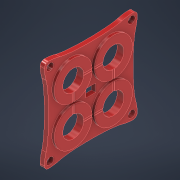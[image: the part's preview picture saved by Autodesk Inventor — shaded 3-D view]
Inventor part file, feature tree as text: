
AUTODESK INVENTOR PART (.ipt)
format: ipt  version: 2022 (Build 260153000, 153)  size: 302,080 bytes
history: native  units: mm
features: extrude x5, projected_geometry x5, sketch x4, fillet x2
ambient origin geometry x8: Origin, YZ Plane, XZ Plane, XY Plane, X Axis, Y Axis, Z Axis, Center Point
bodies: Solid1 (feature_tree)
feature tree (16):
  extrude  "Extrusion1"  Depth=44.0mm
  fillet  "Fillet1"  Radius=38.6mm
  extrude  "Extrusion2"  Depth=3.4mm
  extrude  "Extrusion4"  Depth=3.4mm
  extrude  "Extrusion5"  Depth=2.0mm TaperAngle=0.0deg
  fillet  "Fillet2"  Radius=2.0mm
  extrude  "Extrusion6"  Depth=10.0mm
  sketch  "Sketch2"  dims[d0=44.0mm d1=44.0mm d6=38.6mm]
  projected_geometry  "Projected Loop1"
  sketch  "Sketch4"  dims[d7=38.6mm d8=3.4mm]
  sketch  "Sketch5"  dims[d9=3.4mm d10=3.4mm]
  sketch  "Sketch6"  dims[d11=3.4mm d16=2.0mm d17=0.0mm d18=2.0mm d19=10.0mm d20=10.0mm d21=10.0mm d22=10.0mm d23=19.0mm d24=19.0mm d25=19.0mm d26=19.0mm d27=18.0mm d28=18.0mm d29=18.0mm d30=18.0mm d31=1.2mm d32=0.0mm d36=5.0mm d37=2.0mm d38=0.0mm d39=2.0mm d40=16.0mm d41=2.0mm d42=16.0mm d43=2.0mm d44=16.0mm d45=2.0mm d46=16.0mm d47=2.0mm d48=0.0mm d49=20.0mm d50=4.6mm d51=3.9mm d52=9.2mm d53=1.0mm d54=1.0mm d55=9.2mm d56=9.2mm d57=1.0mm d58=1.0mm d59=9.2mm d60=0.2mm d61=0.0mm]
  projected_geometry  "Projected Loop2"
  projected_geometry  "Projected Loop3"
  projected_geometry  "Projected Loop4"
  projected_geometry  "Projected Loop5"
